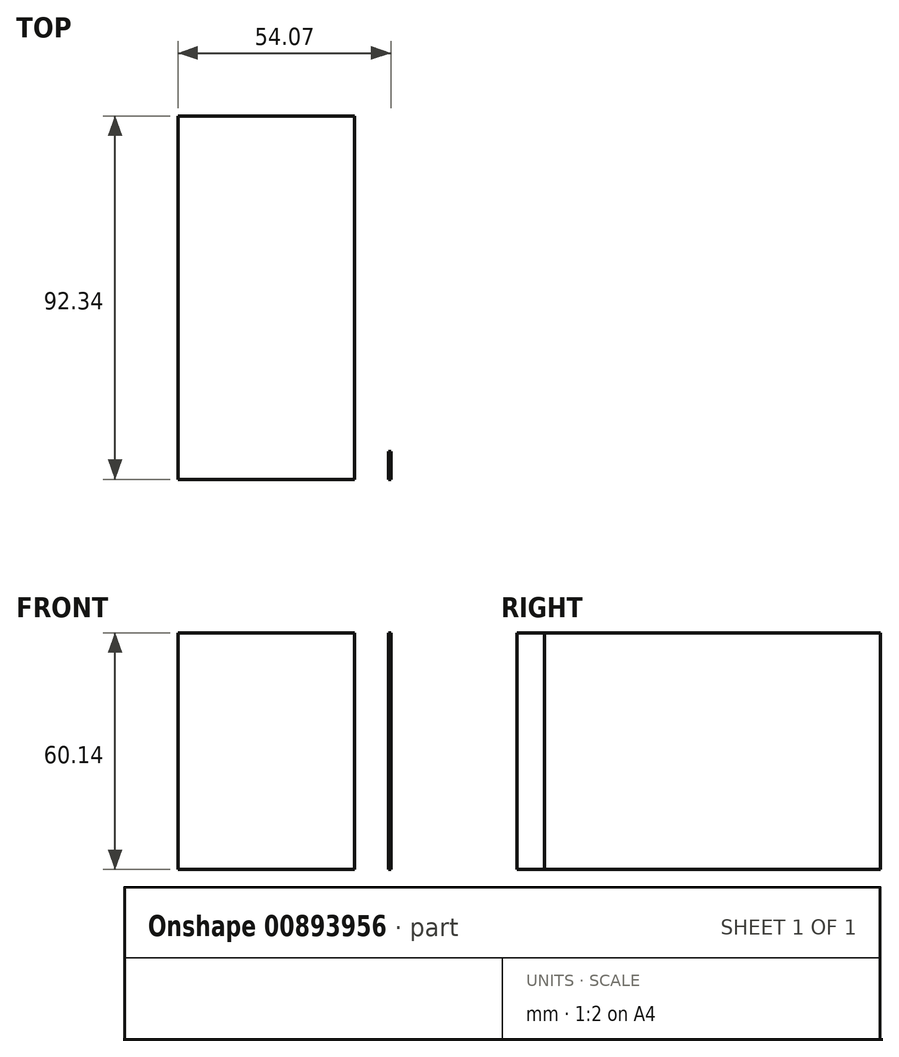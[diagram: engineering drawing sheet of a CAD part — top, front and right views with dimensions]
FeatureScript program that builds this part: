
annotation { "Feature Type Name" : "Feature", "Feature Type Description" : "" }
export const myFeature = defineFeature(function(context is Context, id is Id, definition is map)
    precondition{}
    {
        {
            var Q0;
            Q0=qCreatedBy(makeId("Top.planeOp"),FACE);
            var sketch = newSketch(context, id + "F0", { "sketchPlane" : qUnion([Q0])});
            skLineSegment(sketch, "E0.bottom", {"start": v(28.07, 43.33) * mm, "end": v(-16.78, 43.33) * mm});
            skLineSegment(sketch, "E0.top", {"start": v(28.07, -49.01) * mm, "end": v(-16.78, -49.01) * mm});
            skLineSegment(sketch, "E0.left", {"start": v(28.07, 43.33) * mm, "end": v(28.07, -49.01) * mm});
            skLineSegment(sketch, "E0.right", {"start": v(-16.78, 43.33) * mm, "end": v(-16.78, -49.01) * mm});
            skLineSegment(sketch, "E1.bottom", {"start": v(37.3, -41.96) * mm, "end": v(36.74, -41.96) * mm});
            skLineSegment(sketch, "E1.top", {"start": v(37.3, -49.01) * mm, "end": v(36.74, -49.01) * mm});
            skLineSegment(sketch, "E1.left", {"start": v(37.3, -41.96) * mm, "end": v(37.3, -49.01) * mm});
            skLineSegment(sketch, "E1.right", {"start": v(36.74, -41.96) * mm, "end": v(36.74, -49.01) * mm});
            skSolve(sketch);
        }
        {
            var Q0;
            Q0 = qSketchRegion(id + "F0", true);
            extrude(context, id + "F1", {"entities" : qUnion([Q0]), "depth" : 60.14 * mm, "offsetDistance" : 25.4 * mm});
        }
    });
